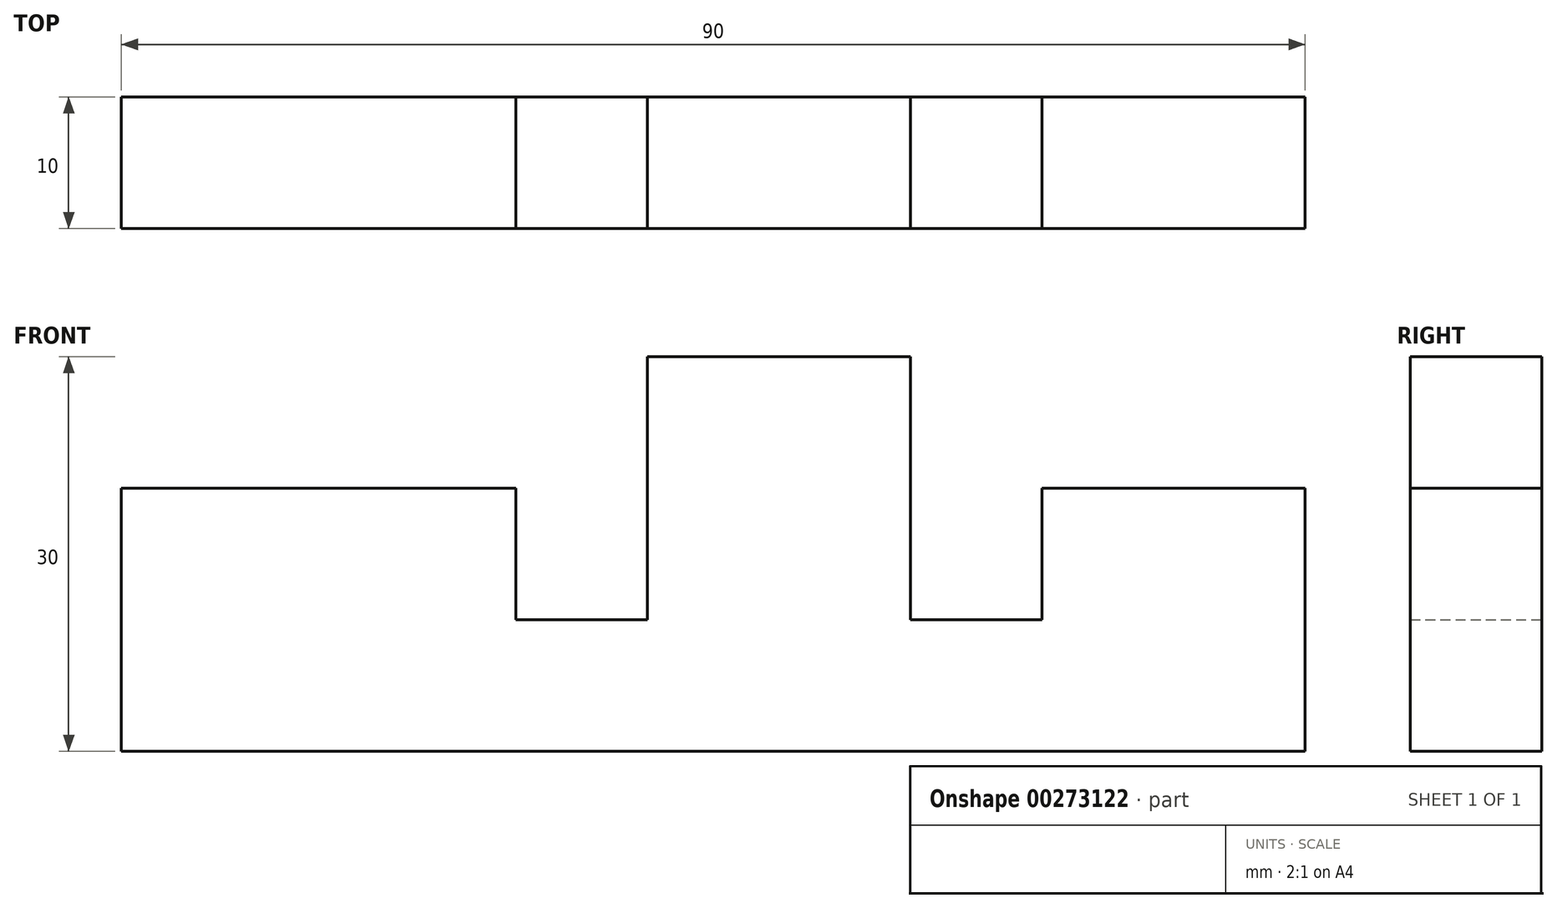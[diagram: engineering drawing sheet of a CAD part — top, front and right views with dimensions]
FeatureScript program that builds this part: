
annotation { "Feature Type Name" : "Feature", "Feature Type Description" : "" }
export const myFeature = defineFeature(function(context is Context, id is Id, definition is map)
    precondition{}
    {
        {
            var Q0;
            Q0=qCreatedBy(makeId("Front.planeOp"),FACE);
            var sketch = newSketch(context, id + "F0", { "sketchPlane" : qUnion([Q0])});
            skLineSegment(sketch, "E0", {"start": v(0, 0) * mm, "end": v(0, 20) * mm});
            skLineSegment(sketch, "E1", {"start": v(0, 20) * mm, "end": v(30, 20) * mm});
            skLineSegment(sketch, "E2", {"start": v(0, 0) * mm, "end": v(90, 0) * mm});
            skLineSegment(sketch, "E3", {"start": v(90, 0) * mm, "end": v(90, 20) * mm});
            skLineSegment(sketch, "E4", {"start": v(30, 20) * mm, "end": v(30, 10) * mm});
            skLineSegment(sketch, "E5", {"start": v(30, 10) * mm, "end": v(40, 10) * mm});
            skLineSegment(sketch, "E6", {"start": v(40, 10) * mm, "end": v(40, 30) * mm});
            skLineSegment(sketch, "E7", {"start": v(40, 30) * mm, "end": v(60, 30) * mm});
            skLineSegment(sketch, "E8", {"start": v(60, 30) * mm, "end": v(60, 10) * mm});
            skLineSegment(sketch, "E9", {"start": v(60, 10) * mm, "end": v(70, 10) * mm});
            skLineSegment(sketch, "E10", {"start": v(70, 10) * mm, "end": v(70, 20) * mm});
            skLineSegment(sketch, "E11", {"start": v(70, 20) * mm, "end": v(90, 20) * mm});
            skSolve(sketch);
        }
        {
            var Q0;
            Q0=makeQuery(id+"F0.imprint","IMPRINT",FACE,{"disambiguationData":[TD([[makeQuery(id+"F0.imprint","IMPRINT",EDGE,{"derivedFrom":sQuery(id+"F0.wireOp",EDGE,"E0")}),-1.0]])]});
            extrude(context, id + "F1", {"entities" : qUnion([Q0]), "depth" : 10 * mm});
        }
    });
